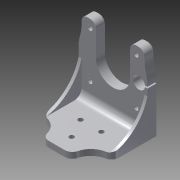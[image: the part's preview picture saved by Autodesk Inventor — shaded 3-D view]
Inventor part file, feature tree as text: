
AUTODESK INVENTOR PART (.ipt)
format: ipt  version: 2015 SP1 (Build 190203100, 203)  size: 294,912 bytes
history: native  units: mm
features: reference x13, sketch x12, extrude x11, fillet x6, projected_geometry x6, hole x4
ambient origin geometry x8: Origin, YZ Plane, XZ Plane, XY Plane, X Axis, Y Axis, Z Axis, Center Point
bodies: Body1 (feature_tree)
feature tree (52):
  hole  "hole points"  [1 undecoded]
  extrude  "back plate Extrusion2"  Depth=4.0mm
  hole  "Hole3"  [1 undecoded]
  extrude  "Extrusion3"  Depth=8.0mm
  extrude  "Extrusion4"  Depth=4.0mm
  extrude  "Extrusion5"  Depth=42.3mm
  hole  "Hole4"  [1 undecoded]
  extrude  "Extrusion6"  Depth=10.0mm
  hole  "Hole5"  [1 undecoded]
  extrude  "Extrusion7"  Depth=1.0mm
  extrude  "Extrusion8"  Depth=6.0mm
  extrude  "Extrusion9"  Depth=5.0mm TaperAngle=0.0deg
  fillet  "Fillet3"  Radius=3.3mm
  fillet  "Fillet6"  Radius=5.0mm
  extrude  "Extrusion12"  Depth=4.0mm
  extrude  "Extrusion13"  Depth=5.0mm
  fillet  "Fillet10"  Radius=30.0mm
  fillet  "Fillet11"  Radius=2.0mm
  extrude  "Extrusion14"  Depth=2.0mm TaperAngle=0.0deg
  fillet  "Fillet14"  Radius=12.0mm
  fillet  "Fillet15"  Radius=5.0mm
  sketch  "Sketch4"  dims[d0=14.0mm d1=13.0mm]
  reference  "Reference1"
  sketch  "Sketch5"  dims[d21=4.0mm d22=0.0mm d31=18.0mm]
  reference  "Reference2"
  sketch  "Sketch6"  dims[d32=4.0mm d33=4.0mm]
  reference  "Reference3"
  reference  "Reference4"
  reference  "Reference5"
  reference  "Reference6"
  reference  "Reference7"
  sketch  "Sketch7"  dims[d34=17.0mm d35=8.0mm]
  reference  "Reference8"
  reference  "Reference9"
  reference  "Reference10"
  reference  "Reference11"
  sketch  "Sketch8"  dims[d36=8.0mm]
  reference  "Reference12"
  sketch  "Sketch9"  dims[d37=3.2mm d38=6.0mm d39=4.0mm d40=2.0mm d41=90.0deg d42=8.0mm d43=20.594885mm d44=4.0mm]
  reference  "Reference13"
  sketch  "Sketch10"  dims[d45=10.0mm d46=0.0mm d47=42.3mm]
  projected_geometry  "Projected Loop1"
  sketch  "Sketch11"  dims[d48=48.0mm d49=0.0mm d50=1.0mm]
  projected_geometry  "Projected Loop2"
  sketch  "Sketch12"  dims[d53=50.0mm d54=0.0mm]
  projected_geometry  "Projected Loop3"
  sketch  "Sketch15"  dims[d55=3.2mm d56=6.0mm d57=4.0mm d58=2.0mm d59=90.0deg d60=8.0mm d61=20.594885mm d62=10.0mm]
  projected_geometry  "Projected Loop4"
  sketch  "Sketch16"  dims[d63=6.0mm d64=2.0mm d65=0.0mm]
  projected_geometry  "Projected Loop5"
  sketch  "Sketch17"  dims[d66=17.5mm d67=8.0mm d68=6.0mm d69=4.0mm d70=2.0mm d71=90.0deg d72=8.0mm d73=20.594885mm d74=1.0mm d75=6.0mm d76=5.0mm d77=0.0mm d78=3.3mm d79=0.0mm d80=5.0mm d81=0.0mm d93=4.0mm d96=5.0mm d97=30.0mm d98=2.0mm d99=0.0mm d100=2.0mm d101=0.0mm d105=12.0mm d106=5.0mm d109=5.5mm d110=0.0mm d111=25.0mm d112=20.0mm]
  projected_geometry  "Projected Loop6"
note: 4 required parameter values undecoded (feature->parameter linkage not recoverable at this tier; creation-order binding heuristic only, values carry confidence <= 0.55)
